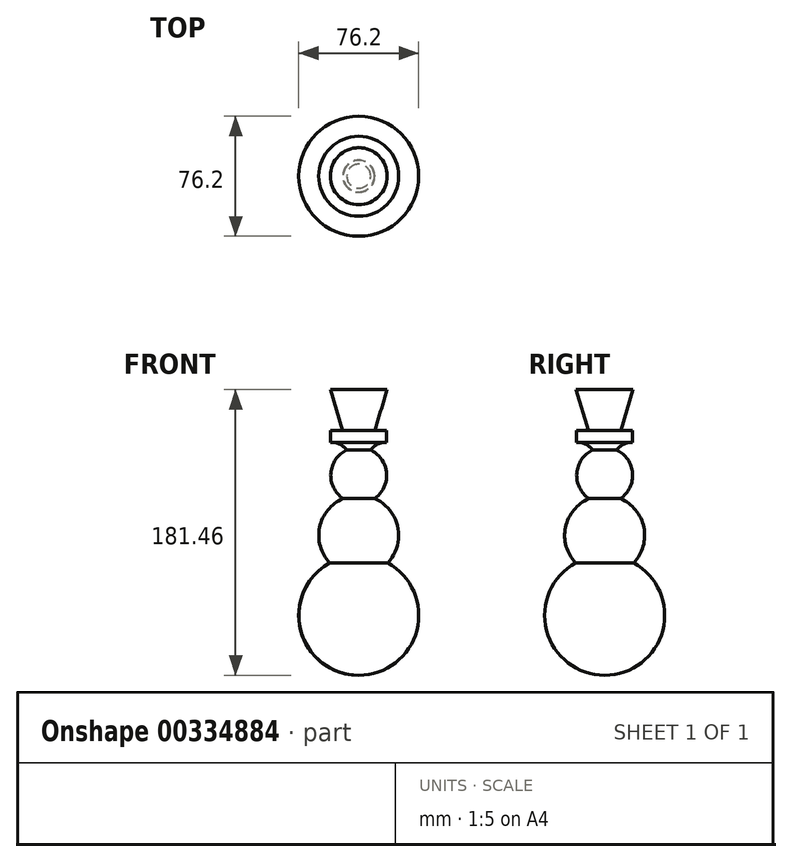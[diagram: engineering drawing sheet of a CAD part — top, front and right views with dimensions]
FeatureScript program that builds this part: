
annotation { "Feature Type Name" : "Feature", "Feature Type Description" : "" }
export const myFeature = defineFeature(function(context is Context, id is Id, definition is map)
    precondition{}
    {
        {
            var Q0;
            Q0=qCreatedBy(makeId("Front.planeOp"),FACE);
            var sketch = newSketch(context, id + "F0", { "sketchPlane" : qUnion([Q0])});
            skArc(sketch, "E0", {"start": v(0, -38.1) * mm, "mid": v(36.9, -9.52) * mm, "end": v(18.45, 33.34) * mm});
            skLineSegment(sketch, "E1", {"start": v(17.78, 109.94) * mm, "end": v(17.78, 117.56) * mm});
            skLineSegment(sketch, "E2", {"start": v(17.78, 117.56) * mm, "end": v(10.2, 117.56) * mm});
            skLineSegment(sketch, "E3", {"start": v(10.2, 117.56) * mm, "end": v(18.09, 143.36) * mm});
            skLineSegment(sketch, "E4", {"start": v(18.09, 143.36) * mm, "end": v(0, 143.36) * mm});
            skArc(sketch, "E5.trimOffspring", {"start": v(9.95, 74.17) * mm, "mid": v(17.73, 90.24) * mm, "end": v(7.63, 104.96) * mm});
            skArc(sketch, "E6.trimOffspring", {"start": v(18.45, 33.34) * mm, "mid": v(24.87, 55.97) * mm, "end": v(9.95, 74.17) * mm});
            skLineSegment(sketch, "E7", {"start": v(0, 143.36) * mm, "end": v(0, 0) * mm});
            skLineSegment(sketch, "E8", {"start": v(0, 0) * mm, "end": v(0, -38.1) * mm});
            skArc(sketch, "E9", {"start": v(17.78, 109.94) * mm, "mid": v(12.06, 108.76) * mm, "end": v(7.63, 104.96) * mm});
            skSolve(sketch);
        }
        {
            var Q0;
            Q0=makeQuery(id+"F0.imprint","IMPRINT",FACE,{"disambiguationData":[TD([[makeQuery(id+"F0.imprint","IMPRINT",EDGE,{"derivedFrom":sQuery(id+"F0.wireOp",EDGE,"E0")}),1.0]])]});
            var Q1;
            {var subQ0=sQuery(id+"F0.wireOp",EDGE,"jvStP1SZ-PqVW-Mzqt-xwpC-jKYrI5NjSmrC");Q1=makeQuery(id+"F0.imprint","IMPRINT",FACE,{"disambiguationData":[TD([[makeQuery(id+"F0.imprint","IMPRINT",EDGE,{"derivedFrom":subQ0}),1.0]])]});}
            var Q2;
            Q2=sQuery(id+"F0.wireOp",EDGE,"E7");
            revolve(context, id + "F1", {"entities" : qUnion([Q0, Q1]), "axis" : qUnion([Q2]), "revolveType" : RevolveType.FULL});
        }
    });
